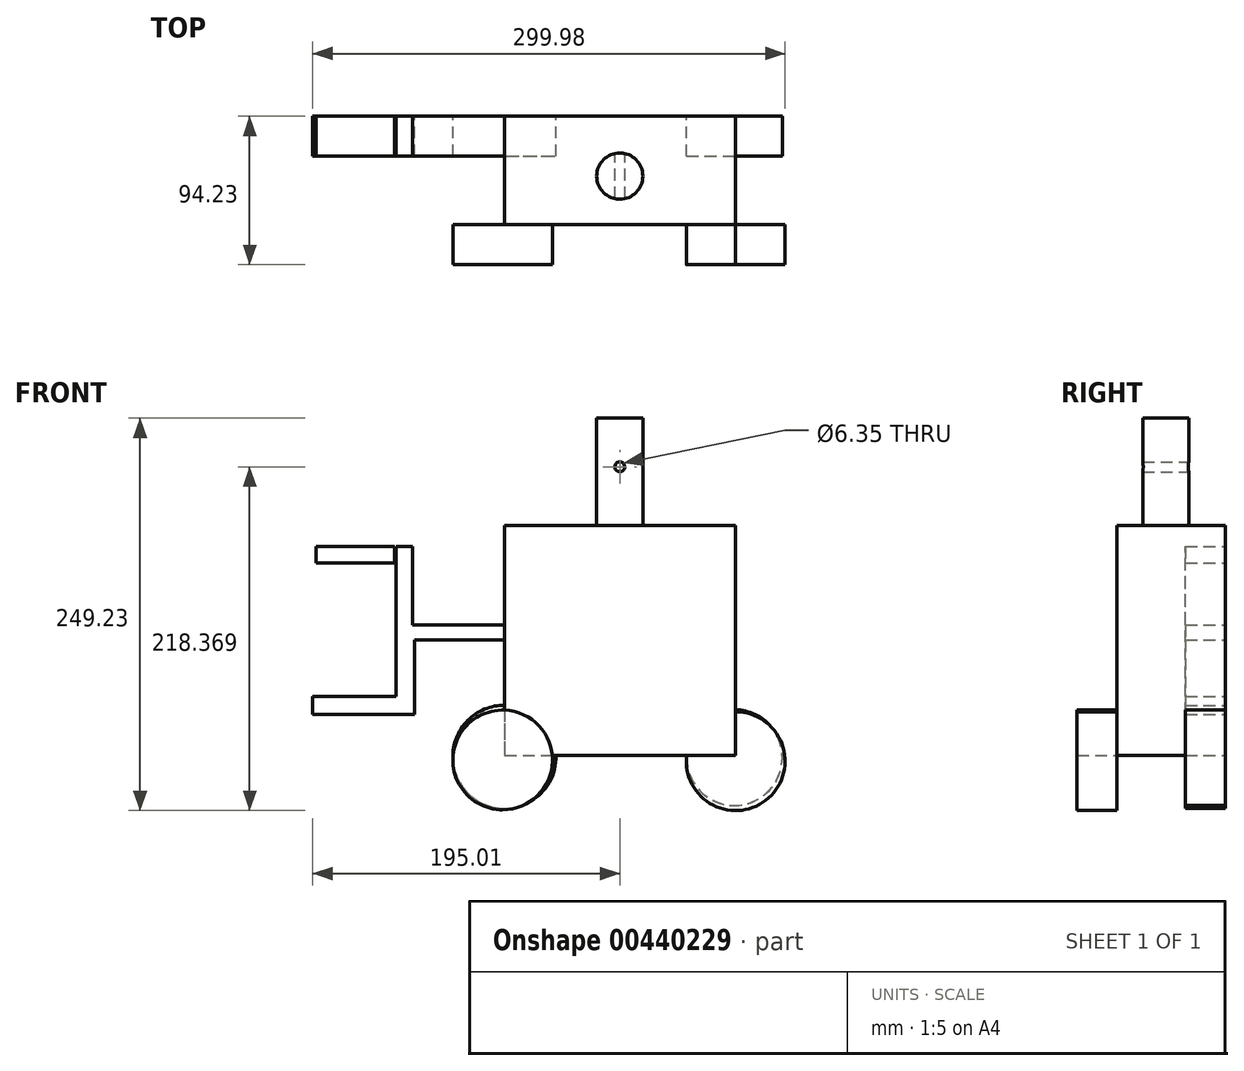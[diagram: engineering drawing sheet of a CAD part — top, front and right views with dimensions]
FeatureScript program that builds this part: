
annotation { "Feature Type Name" : "Feature", "Feature Type Description" : "" }
export const myFeature = defineFeature(function(context is Context, id is Id, definition is map)
    precondition{}
    {
        {
            var Q0;
            Q0=qCreatedBy(makeId("Front.planeOp"),FACE);
            var sketch = newSketch(context, id + "F0", { "sketchPlane" : qUnion([Q0])});
            skLineSegment(sketch, "E0.bottom", {"start": v(-73.06, 72.96) * mm, "end": v(73.6, 72.96) * mm});
            skLineSegment(sketch, "E0.top", {"start": v(-73.06, -73.34) * mm, "end": v(73.6, -73.34) * mm});
            skLineSegment(sketch, "E0.left", {"start": v(-73.06, 72.96) * mm, "end": v(-73.06, -73.34) * mm});
            skLineSegment(sketch, "E0.right", {"start": v(73.6, 72.96) * mm, "end": v(73.6, -73.34) * mm});
            skSolve(sketch);
        }
        {
            var Q0;
            Q0 = qSketchRegion(id + "F0", true);
            extrude(context, id + "F1", {"entities" : qUnion([Q0]), "depth" : 68.83 * mm});
        }
        {
            var Q0;
            Q0=qCreatedBy(makeId("Top.planeOp"),FACE);
            var sketch = newSketch(context, id + "F2", { "sketchPlane" : qUnion([Q0])});
            skCircle(sketch, "E1", {"center": v(0, -37.95) * mm, "radius": 14.66 * mm});
            skSolve(sketch);
        }
        {
            var Q0;
            Q0 = qSketchRegion(id + "F2", true);
            extrude(context, id + "F3", {"entities" : qUnion([Q0]), "operationType" : NewBodyOperationType.ADD, "depth" : 140.97 * mm});
        }
        {
            var Q0;
            Q0=qCreatedBy(makeId("Front.planeOp"),FACE);
            var sketch = newSketch(context, id + "F4", { "sketchPlane" : qUnion([Q0])});
            skPoint(sketch, "E2", {"position": v(0, 110.1) * mm});
            skSolve(sketch);
        }
        {
            var Q0;
            Q0=sQuery(id+"F4.wireOp",VERTEX,"E2");
            var Q1;
            Q1=makeQuery(id+"F1.opExtrude","SWEPT_BODY",BODY,{"disambiguationData":[OSD([sQuery(id+"F0.wireOp",EDGE,"E0.bottom"),sQuery(id+"F0.wireOp",EDGE,"E0.top"),sQuery(id+"F0.wireOp",EDGE,"E0.left"),sQuery(id+"F0.wireOp",EDGE,"E0.right")])]});
            hole(context, id + "F5", {"style" : HoleStyle.SIMPLE, "endStyle" : HoleEndStyle.THROUGH, "oppositeDirection" : true, "holeDiameter" : 6.35 * mm, "isTappedThrough" : true, "tappedDepth" : 12.7 * mm, "tapClearance" : 3, "locations" : qUnion([Q0]), "scope" : qUnion([Q1])});
        }
        {
            var Q0;
            Q0=makeQuery(id+"F1.opExtrude","CAP_FACE",FACE,{"disambiguationData":[OSD([sQuery(id+"F0.wireOp",EDGE,"E0.bottom"),sQuery(id+"F0.wireOp",EDGE,"E0.top"),sQuery(id+"F0.wireOp",EDGE,"E0.left"),sQuery(id+"F0.wireOp",EDGE,"E0.right")])],"isStart":false});
            var sketch = newSketch(context, id + "F6", { "sketchPlane" : qUnion([Q0])});
            skCircle(sketch, "E3", {"center": v(73.6, -76.89) * mm, "radius": 31.37 * mm});
            skSolve(sketch);
        }
        {
            var Q0;
            {var subQ4=makeQuery(id+"F1.opExtrude","CAP_EDGE",EDGE,{"disambiguationData":[OSD([sQuery(id+"F0.wireOp",EDGE,"E0.bottom")])],"isStart":false});Q0=makeQuery(id+"F6.imprint","IMPRINT",FACE,{"disambiguationData":[TD([[makeQuery(id+"F6.imprint","IMPRINT",EDGE,{"derivedFrom":subQ4}),-1.0]])]});}
            var sketch = newSketch(context, id + "F7", { "sketchPlane" : qUnion([Q0])});
            skCircle(sketch, "E4", {"center": v(-74.39, -76.1) * mm, "radius": 31.67 * mm});
            skSolve(sketch);
        }
        {
            var Q0;
            Q0 = qSketchRegion(id + "F7", true);
            extrude(context, id + "F8", {"entities" : qUnion([Q0]), "operationType" : NewBodyOperationType.ADD, "depth" : 25.4 * mm});
        }
        {
            var Q0;
            {var subQ0=sQuery(id+"F6.wireOp",EDGE,"E3");var subQ1=makeQuery(id+"F1.opExtrude","CAP_EDGE",EDGE,{"disambiguationData":[OSD([sQuery(id+"F0.wireOp",EDGE,"E0.top")])],"isStart":false});var subQ2=makeQuery(id+"F6.imprint","INTERSECT",VERTEX,{"derivedFrom":[subQ1,subQ0]});Q0=makeQuery(id+"F6.imprint","IMPRINT",FACE,{"disambiguationData":[TD([[makeQuery(id+"F6.imprint","IMPRINT",EDGE,{"disambiguationData":[TD([[subQ2,-1.0]])],"derivedFrom":subQ0}),1.0]])]});}
            extrude(context, id + "F9", {"entities" : qUnion([Q0]), "depth" : 25.4 * mm});
        }
        {
            var Q0;
            Q0=qCreatedBy(makeId("Front.planeOp"),FACE);
            var sketch = newSketch(context, id + "F10", { "sketchPlane" : qUnion([Q0])});
            skCircle(sketch, "E5", {"center": v(72.8, -74.61) * mm, "radius": 30.4 * mm});
            skCircle(sketch, "E6", {"center": v(-73.25, -74.11) * mm, "radius": 32.8 * mm});
            skSolve(sketch);
        }
        {
            var Q0;
            Q0 = qSketchRegion(id + "F10", true);
            extrude(context, id + "F11", {"entities" : qUnion([Q0]), "operationType" : NewBodyOperationType.ADD, "depth" : 25.4 * mm});
        }
        {
            var Q0;
            Q0=qCreatedBy(makeId("Front.planeOp"),FACE);
            var sketch = newSketch(context, id + "F12", { "sketchPlane" : qUnion([Q0])});
            skLineSegment(sketch, "E7.bottom", {"start": v(-72.4, 0) * mm, "end": v(-142.18, 0) * mm});
            skLineSegment(sketch, "E7.top", {"start": v(-72.4, 9.63) * mm, "end": v(-142.18, 9.63) * mm});
            skLineSegment(sketch, "E7.left", {"start": v(-72.4, 0) * mm, "end": v(-72.4, 9.63) * mm});
            skLineSegment(sketch, "E7.right", {"start": v(-142.18, 0) * mm, "end": v(-142.18, 9.63) * mm});
            skLineSegment(sketch, "E8.bottom", {"start": v(-142.18, 9.63) * mm, "end": v(-131.7, 9.63) * mm});
            skLineSegment(sketch, "E8.top", {"start": v(-142.18, 59.47) * mm, "end": v(-131.7, 59.47) * mm});
            skLineSegment(sketch, "E8.left", {"start": v(-142.18, 9.63) * mm, "end": v(-142.18, 59.47) * mm});
            skLineSegment(sketch, "E8.right", {"start": v(-131.7, 9.63) * mm, "end": v(-131.7, 59.47) * mm});
            skLineSegment(sketch, "E9.bottom", {"start": v(-143.17, 59.47) * mm, "end": v(-193.02, 59.47) * mm});
            skLineSegment(sketch, "E9.top", {"start": v(-143.17, 49) * mm, "end": v(-193.02, 49) * mm});
            skLineSegment(sketch, "E9.left", {"start": v(-143.17, 59.47) * mm, "end": v(-143.17, 49) * mm});
            skLineSegment(sketch, "E9.right", {"start": v(-193.02, 59.47) * mm, "end": v(-193.02, 49) * mm});
            skLineSegment(sketch, "E10.bottom", {"start": v(-142.18, 0) * mm, "end": v(-130.21, 0) * mm});
            skLineSegment(sketch, "E10.top", {"start": v(-142.18, -47.2) * mm, "end": v(-130.21, -47.2) * mm});
            skLineSegment(sketch, "E10.left", {"start": v(-142.18, 0) * mm, "end": v(-142.18, -47.2) * mm});
            skLineSegment(sketch, "E10.right", {"start": v(-130.21, 0) * mm, "end": v(-130.21, -47.2) * mm});
            skLineSegment(sketch, "E11.bottom", {"start": v(-142.18, -47.2) * mm, "end": v(-195.01, -47.2) * mm});
            skLineSegment(sketch, "E11.top", {"start": v(-142.18, -35.73) * mm, "end": v(-195.01, -35.73) * mm});
            skLineSegment(sketch, "E11.left", {"start": v(-142.18, -47.2) * mm, "end": v(-142.18, -35.73) * mm});
            skLineSegment(sketch, "E11.right", {"start": v(-195.01, -47.2) * mm, "end": v(-195.01, -35.73) * mm});
            skSolve(sketch);
        }
        {
            var Q0;
            Q0 = qSketchRegion(id + "F12", true);
            extrude(context, id + "F13", {"entities" : qUnion([Q0]), "operationType" : NewBodyOperationType.ADD, "depth" : 25.4 * mm});
        }
    });
